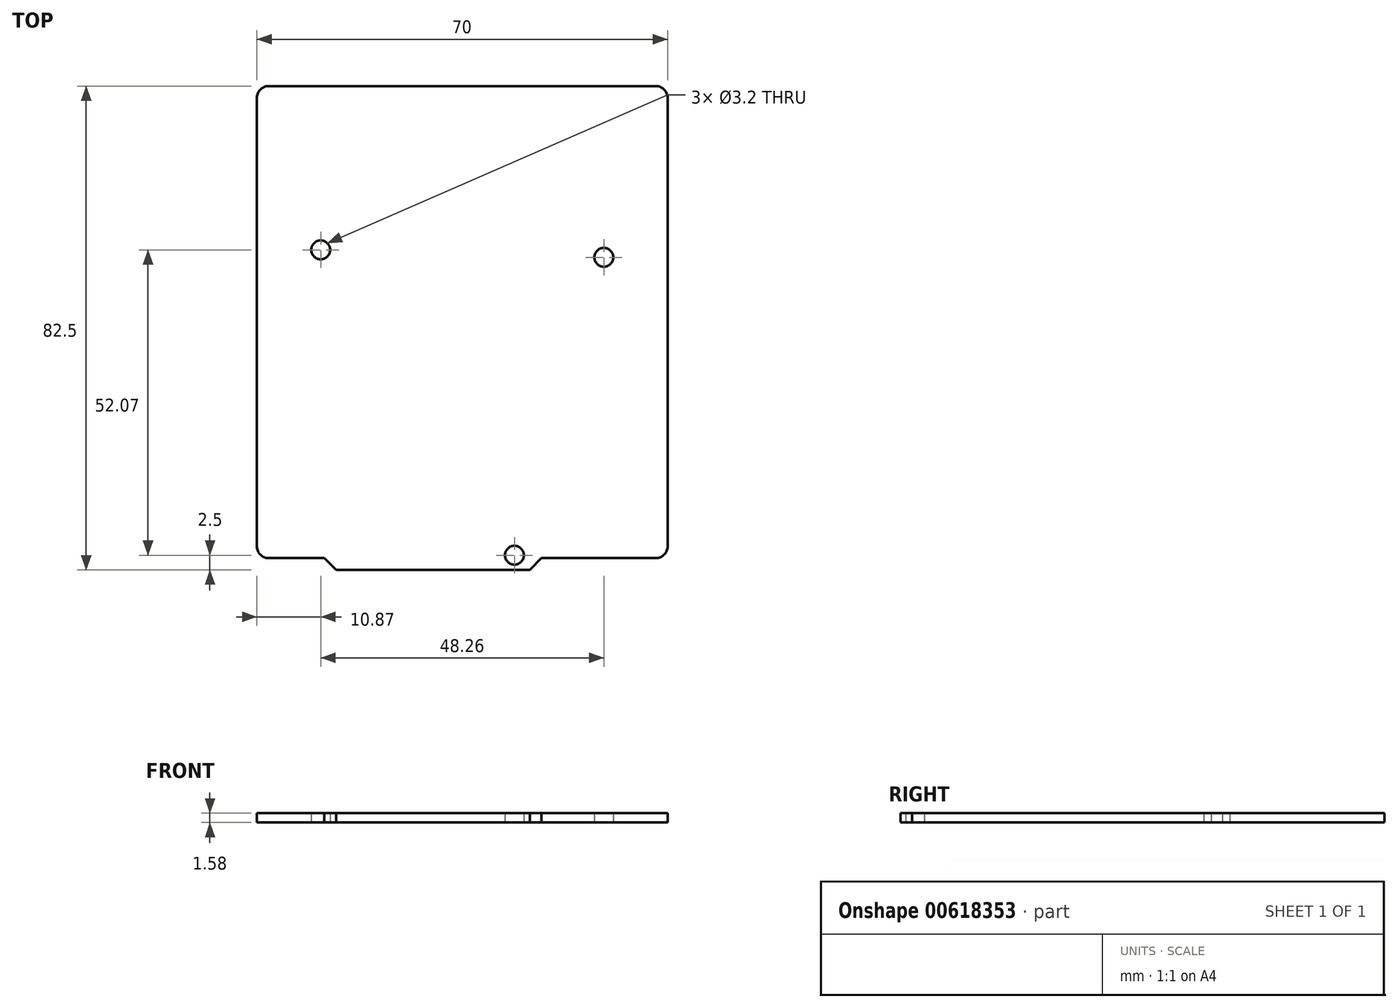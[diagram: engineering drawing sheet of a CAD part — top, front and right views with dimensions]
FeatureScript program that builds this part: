
annotation { "Feature Type Name" : "Feature", "Feature Type Description" : "" }
export const myFeature = defineFeature(function(context is Context, id is Id, definition is map)
    precondition{}
    {
        {
            var Q0;
            Q0=qCreatedBy(makeId("Top.planeOp"),FACE);
            var sketch = newSketch(context, id + "F0", { "sketchPlane" : qUnion([Q0])});
            skLineSegment(sketch, "E0.bottom", {"start": v(35, -40.25) * mm, "end": v(13.5, -40.25) * mm});
            skLineSegment(sketch, "E0.top", {"start": v(35, 40.25) * mm, "end": v(-35, 40.25) * mm});
            skLineSegment(sketch, "E0.left", {"start": v(35, -40.25) * mm, "end": v(35, 40.25) * mm});
            skLineSegment(sketch, "E0.right", {"start": v(-35, -40.25) * mm, "end": v(-35, 40.25) * mm});
            skPoint(sketch, "E0.middle", {"position": v(0, 0) * mm});
            skLineSegment(sketch, "E1", {"start": v(-21.5, -42.25) * mm, "end": v(11.5, -42.25) * mm});
            skLineSegment(sketch, "E2", {"start": v(13.5, -40.25) * mm, "end": v(11.5, -42.25) * mm});
            skLineSegment(sketch, "E3", {"start": v(-21.5, -42.25) * mm, "end": v(-23.5, -40.25) * mm});
            skLineSegment(sketch, "E4.trimOffspring", {"start": v(-23.5, -40.25) * mm, "end": v(-35, -40.25) * mm});
            skPoint(sketch, "E5", {"position": v(-24.13, 12.32) * mm});
            skPoint(sketch, "E6", {"position": v(24.13, 11.05) * mm});
            skPoint(sketch, "E7", {"position": v(8.89, -39.75) * mm});
            skSolve(sketch);
        }
        {
            var Q0;
            Q0=makeQuery(id+"F0.imprint","IMPRINT",FACE,{"disambiguationData":[TD([[makeQuery(id+"F0.imprint","IMPRINT",EDGE,{"derivedFrom":sQuery(id+"F0.wireOp",EDGE,"E0.bottom")}),-1.0]])]});
            extrude(context, id + "F1", {"entities" : qUnion([Q0]), "depth" : 1.58 * mm, "offsetDistance" : 25 * mm});
        }
        {
            var Q0;
            Q0=makeQuery(id+"F1.opExtrude","SWEPT_EDGE",EDGE,{"disambiguationData":[OSD([sQuery(id+"F0.wireOp",EDGE,"E0.top"),sQuery(id+"F0.wireOp",EDGE,"E0.right")])]});
            var Q1;
            Q1=makeQuery(id+"F1.opExtrude","SWEPT_EDGE",EDGE,{"disambiguationData":[OSD([sQuery(id+"F0.wireOp",EDGE,"E0.top"),sQuery(id+"F0.wireOp",EDGE,"E0.left")])]});
            var Q2;
            Q2=makeQuery(id+"F1.opExtrude","SWEPT_EDGE",EDGE,{"disambiguationData":[OSD([sQuery(id+"F0.wireOp",EDGE,"E0.right"),sQuery(id+"F0.wireOp",EDGE,"E4.trimOffspring")])]});
            var Q3;
            Q3=makeQuery(id+"F1.opExtrude","SWEPT_EDGE",EDGE,{"disambiguationData":[OSD([sQuery(id+"F0.wireOp",EDGE,"E0.bottom"),sQuery(id+"F0.wireOp",EDGE,"E0.left")])]});
            fillet(context, id + "F2", {"entities" : qUnion([Q0, Q1, Q2, Q3]), "radius" : 2 * mm, "tangentPropagation" : true, "allowEdgeOverflow" : false});
        }
        {
            var Q0;
            Q0=sQuery(id+"F0.wireOp",VERTEX,"E5");
            var Q1;
            Q1=sQuery(id+"F0.wireOp",VERTEX,"E6");
            var Q2;
            Q2=sQuery(id+"F0.wireOp",VERTEX,"E7");
            var Q3;
            Q3=makeQuery(id+"F1.opExtrude","SWEPT_BODY",BODY,{"disambiguationData":[OSD([sQuery(id+"F0.wireOp",EDGE,"E0.bottom"),sQuery(id+"F0.wireOp",EDGE,"E0.top"),sQuery(id+"F0.wireOp",EDGE,"E0.left"),sQuery(id+"F0.wireOp",EDGE,"E0.right"),sQuery(id+"F0.wireOp",EDGE,"E1"),sQuery(id+"F0.wireOp",EDGE,"E2"),sQuery(id+"F0.wireOp",EDGE,"E3"),sQuery(id+"F0.wireOp",EDGE,"E4.trimOffspring")])]});
            hole(context, id + "F3", {"style" : HoleStyle.SIMPLE, "endStyle" : HoleEndStyle.THROUGH, "oppositeDirection" : true, "holeDiameter" : 3.2 * mm, "majorDiameter" : 5 * mm, "isTappedThrough" : true, "tappedDepth" : 2.3 * mm, "tapClearance" : 3, "startFromSketch" : true, "locations" : qUnion([Q0, Q1, Q2]), "scope" : qUnion([Q3])});
        }
    });
